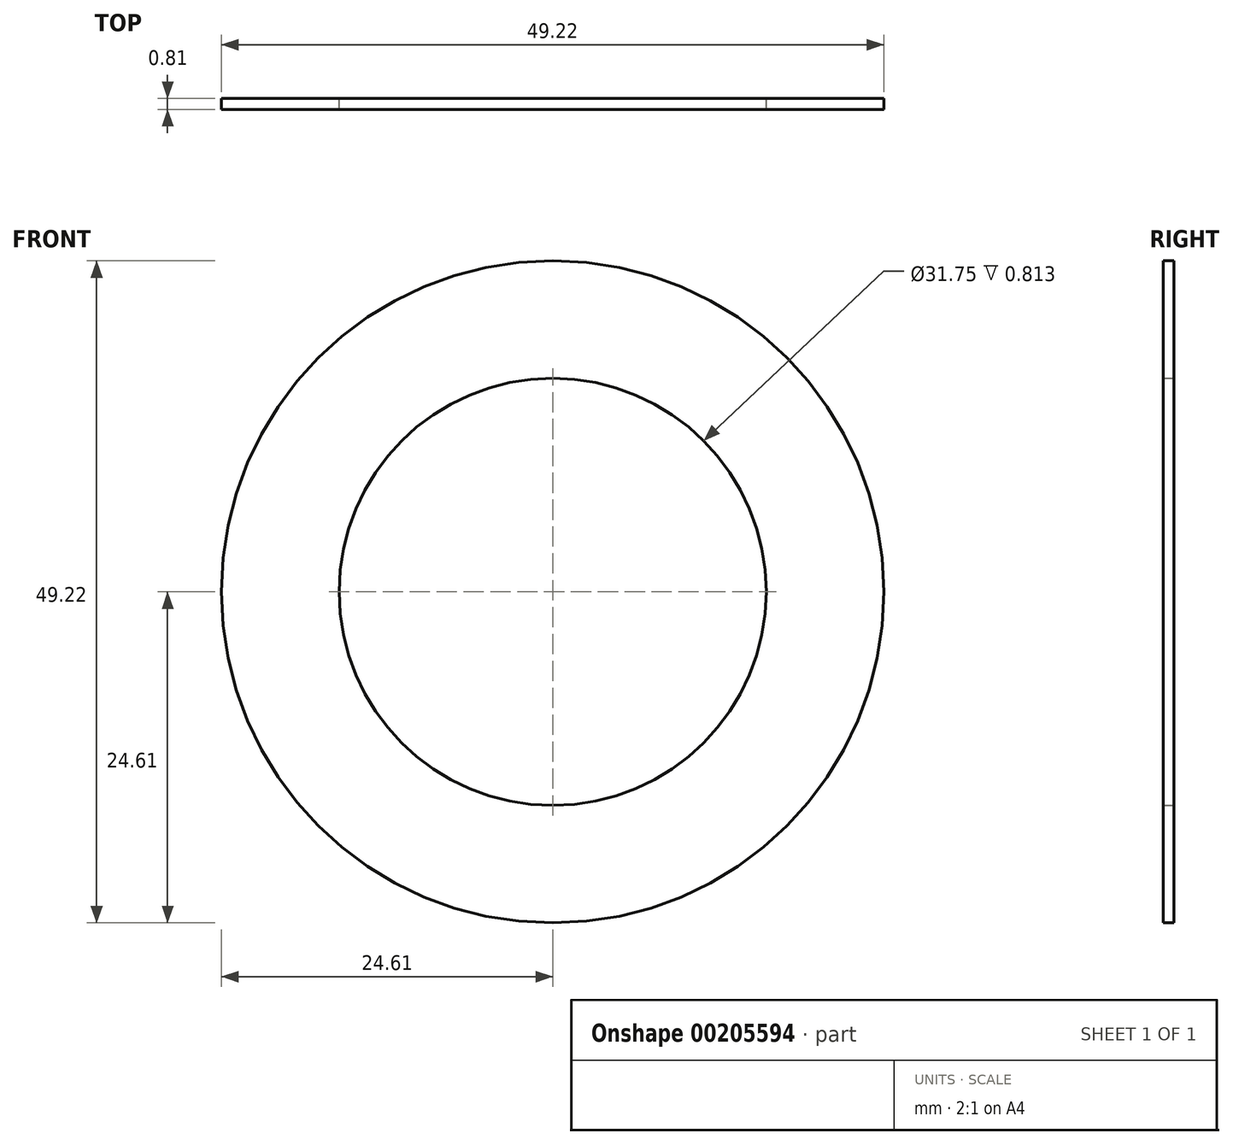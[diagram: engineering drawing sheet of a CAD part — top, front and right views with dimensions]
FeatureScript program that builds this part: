
annotation { "Feature Type Name" : "Feature", "Feature Type Description" : "" }
export const myFeature = defineFeature(function(context is Context, id is Id, definition is map)
    precondition{}
    {
        {
            var Q0;
            Q0=qCreatedBy(makeId("Front.planeOp"),FACE);
            var sketch = newSketch(context, id + "F0", { "sketchPlane" : qUnion([Q0])});
            skCircle(sketch, "E0", {"center": v(0, 0) * mm, "radius": 15.88 * mm});
            skCircle(sketch, "E1", {"center": v(0, 0) * mm, "radius": 24.61 * mm});
            skSolve(sketch);
        }
        {
            var Q0;
            Q0=qSketchRegion(id+"F0",true);
            extrude(context, id + "F1", {"entities" : qUnion([Q0]), "depth" : 0.81 * mm});
        }
    });
